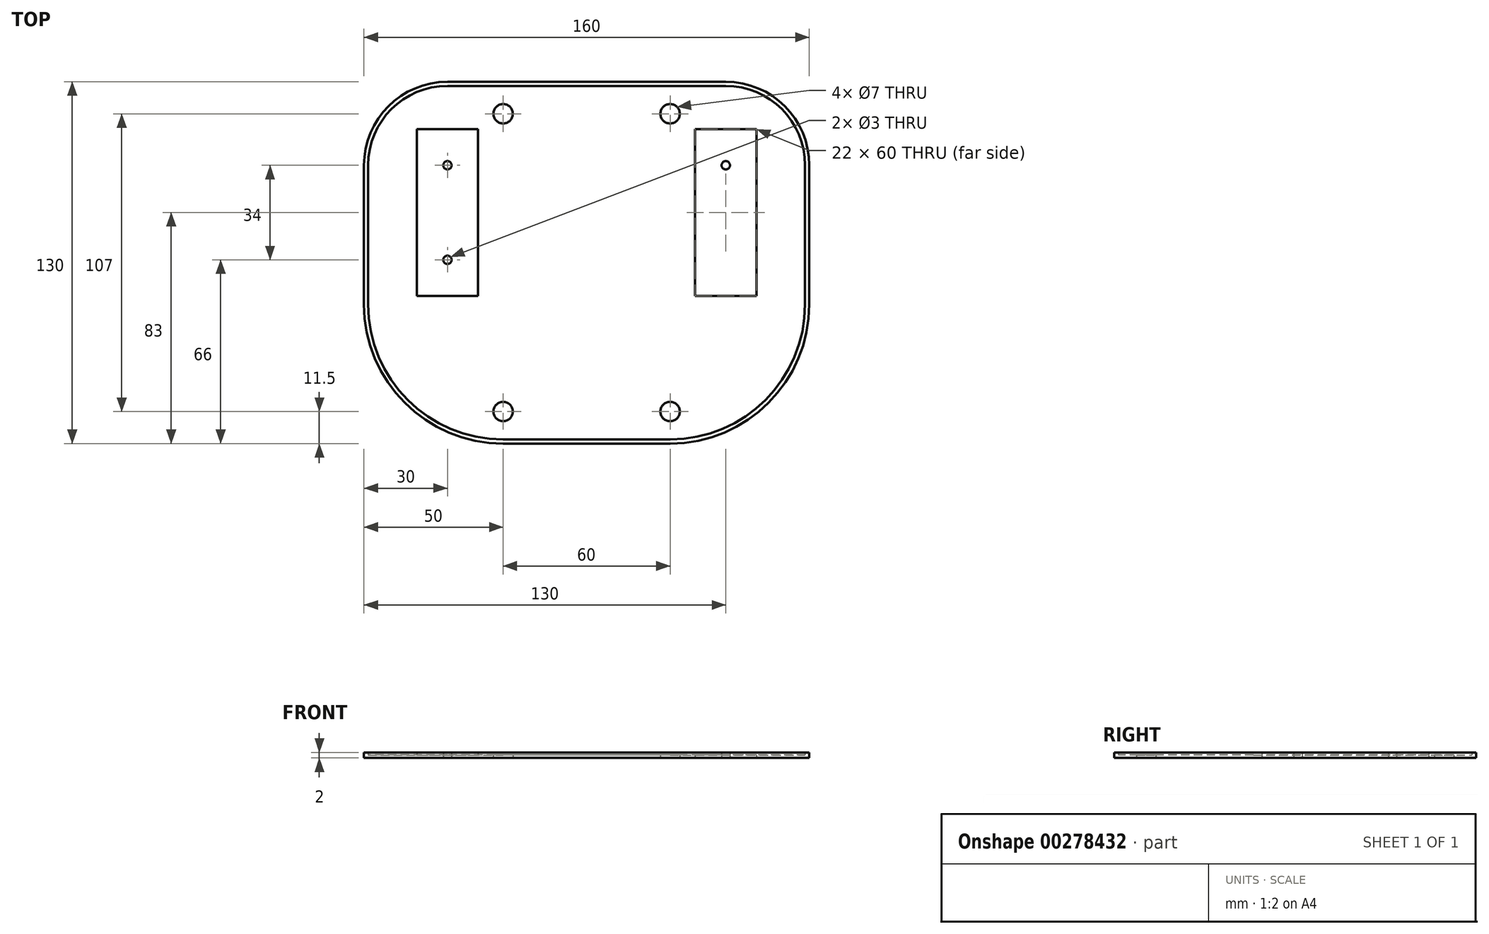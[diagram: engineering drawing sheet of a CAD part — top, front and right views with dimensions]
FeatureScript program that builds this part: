
annotation { "Feature Type Name" : "Feature", "Feature Type Description" : "" }
export const myFeature = defineFeature(function(context is Context, id is Id, definition is map)
    precondition{}
    {
        {
            var Q0;
            Q0=qCreatedBy(makeId("Top.planeOp"),FACE);
            var sketch = newSketch(context, id + "F0", { "sketchPlane" : qUnion([Q0])});
            skLineSegment(sketch, "E0.bottom", {"start": v(30, -65) * mm, "end": v(-30, -65) * mm});
            skLineSegment(sketch, "E0.top", {"start": v(50, 65) * mm, "end": v(-50, 65) * mm});
            skLineSegment(sketch, "E0.left", {"start": v(80, -15) * mm, "end": v(80, 35) * mm});
            skLineSegment(sketch, "E0.right", {"start": v(-80, -15) * mm, "end": v(-80, 35) * mm});
            skPoint(sketch, "E0.middle", {"position": v(0, 0) * mm});
            skCircle(sketch, "E1", {"center": v(-50, 35) * mm, "radius": 1.5 * mm});
            skCircle(sketch, "E2", {"center": v(-50, 1) * mm, "radius": 1.5 * mm});
            skCircle(sketch, "E3.MirrorC", {"center": v(50, 35) * mm, "radius": 1.5 * mm});
            skCircle(sketch, "E4.MirrorC", {"center": v(50, 1) * mm, "radius": 1.5 * mm});
            skPoint(sketch, "E5.visualSharp", {"position": v(-80, -65) * mm});
            skArc(sketch, "E5.filletArc", {"start": v(-80, -15) * mm, "mid": v(-65.36, -50.36) * mm, "end": v(-30, -65) * mm});
            skPoint(sketch, "E6.visualSharp", {"position": v(80, -65) * mm});
            skArc(sketch, "E6.filletArc", {"start": v(30, -65) * mm, "mid": v(65.36, -50.36) * mm, "end": v(80, -15) * mm});
            skPoint(sketch, "E7.visualSharp", {"position": v(80, 65) * mm});
            skArc(sketch, "E7.filletArc", {"start": v(80, 35) * mm, "mid": v(71.21, 56.21) * mm, "end": v(50, 65) * mm});
            skPoint(sketch, "E8.visualSharp", {"position": v(-80, 65) * mm});
            skArc(sketch, "E8.filletArc", {"start": v(-50, 65) * mm, "mid": v(-71.21, 56.21) * mm, "end": v(-80, 35) * mm});
            skLineSegment(sketch, "E9.bottom", {"start": v(-61, 48) * mm, "end": v(-39, 48) * mm});
            skLineSegment(sketch, "E9.top", {"start": v(-61, -12) * mm, "end": v(-39, -12) * mm});
            skLineSegment(sketch, "E9.left", {"start": v(-61, 48) * mm, "end": v(-61, -12) * mm});
            skLineSegment(sketch, "E9.right", {"start": v(-39, 48) * mm, "end": v(-39, -12) * mm});
            skLineSegment(sketch, "E10", {"start": v(-50, 48) * mm, "end": v(-50, -12) * mm, "construction": true});
            skLineSegment(sketch, "E11.MirrorCS", {"start": v(39, 48) * mm, "end": v(39, -12) * mm});
            skLineSegment(sketch, "E12.MirrorCS", {"start": v(61, 48) * mm, "end": v(39, 48) * mm});
            skLineSegment(sketch, "E13.MirrorCS", {"start": v(61, 48) * mm, "end": v(61, -12) * mm});
            skLineSegment(sketch, "E14.MirrorCS", {"start": v(61, -12) * mm, "end": v(39, -12) * mm});
            skArc(sketch, "E15.0", {"start": v(78.5, 35) * mm, "mid": v(70.15, 55.15) * mm, "end": v(50, 63.5) * mm});
            skLineSegment(sketch, "E15.1", {"start": v(78.5, -15) * mm, "end": v(78.5, 35) * mm});
            skLineSegment(sketch, "E15.2", {"start": v(50, 63.5) * mm, "end": v(-50, 63.5) * mm});
            skArc(sketch, "E15.3", {"start": v(30, -63.5) * mm, "mid": v(64.3, -49.3) * mm, "end": v(78.5, -15) * mm});
            skArc(sketch, "E15.4", {"start": v(-50, 63.5) * mm, "mid": v(-70.15, 55.15) * mm, "end": v(-78.5, 35) * mm});
            skLineSegment(sketch, "E15.5", {"start": v(-78.5, -15) * mm, "end": v(-78.5, 35) * mm});
            skArc(sketch, "E15.6", {"start": v(-78.5, -15) * mm, "mid": v(-64.3, -49.3) * mm, "end": v(-30, -63.5) * mm});
            skLineSegment(sketch, "E15.7", {"start": v(30, -63.5) * mm, "end": v(-30, -63.5) * mm});
            skCircle(sketch, "E16", {"center": v(30, 53.5) * mm, "radius": 3.5 * mm});
            skCircle(sketch, "E17.MirrorC", {"center": v(-30, 53.5) * mm, "radius": 3.5 * mm});
            skCircle(sketch, "E18.MirrorC", {"center": v(30, -53.5) * mm, "radius": 3.5 * mm});
            skCircle(sketch, "E19.MirrorC", {"center": v(-30, -53.5) * mm, "radius": 3.5 * mm});
            skSolve(sketch);
        }
        {
            var Q0;
            Q0=makeQuery(id+"F0.imprint","IMPRINT",FACE,{"disambiguationData":[TD([[makeQuery(id+"F0.imprint","IMPRINT",EDGE,{"derivedFrom":sQuery(id+"F0.wireOp",EDGE,"E9.bottom")}),1.0]])]});
            extrude(context, id + "F1", {"entities" : qUnion([Q0]), "depth" : 1 * mm});
        }
        {
            var Q0;
            Q0=makeQuery(id+"F0.imprint","IMPRINT",FACE,{"disambiguationData":[TD([[makeQuery(id+"F0.imprint","IMPRINT",EDGE,{"derivedFrom":sQuery(id+"F0.wireOp",EDGE,"E1")}),-1.0]])]});
            var Q1;
            Q1=makeQuery(id+"F0.imprint","IMPRINT",FACE,{"disambiguationData":[TD([[makeQuery(id+"F0.imprint","IMPRINT",EDGE,{"derivedFrom":sQuery(id+"F0.wireOp",EDGE,"E3.MirrorC")}),1.0]])]});
            var Q2;
            Q2=makeQuery(id+"F0.imprint","IMPRINT",FACE,{"disambiguationData":[TD([[makeQuery(id+"F0.imprint","IMPRINT",EDGE,{"derivedFrom":sQuery(id+"F0.wireOp",EDGE,"E0.bottom")}),-1.0]])]});
            extrude(context, id + "F2", {"entities" : qUnion([Q0, Q1, Q2]), "operationType" : NewBodyOperationType.ADD, "depth" : 2 * mm});
        }
    });
